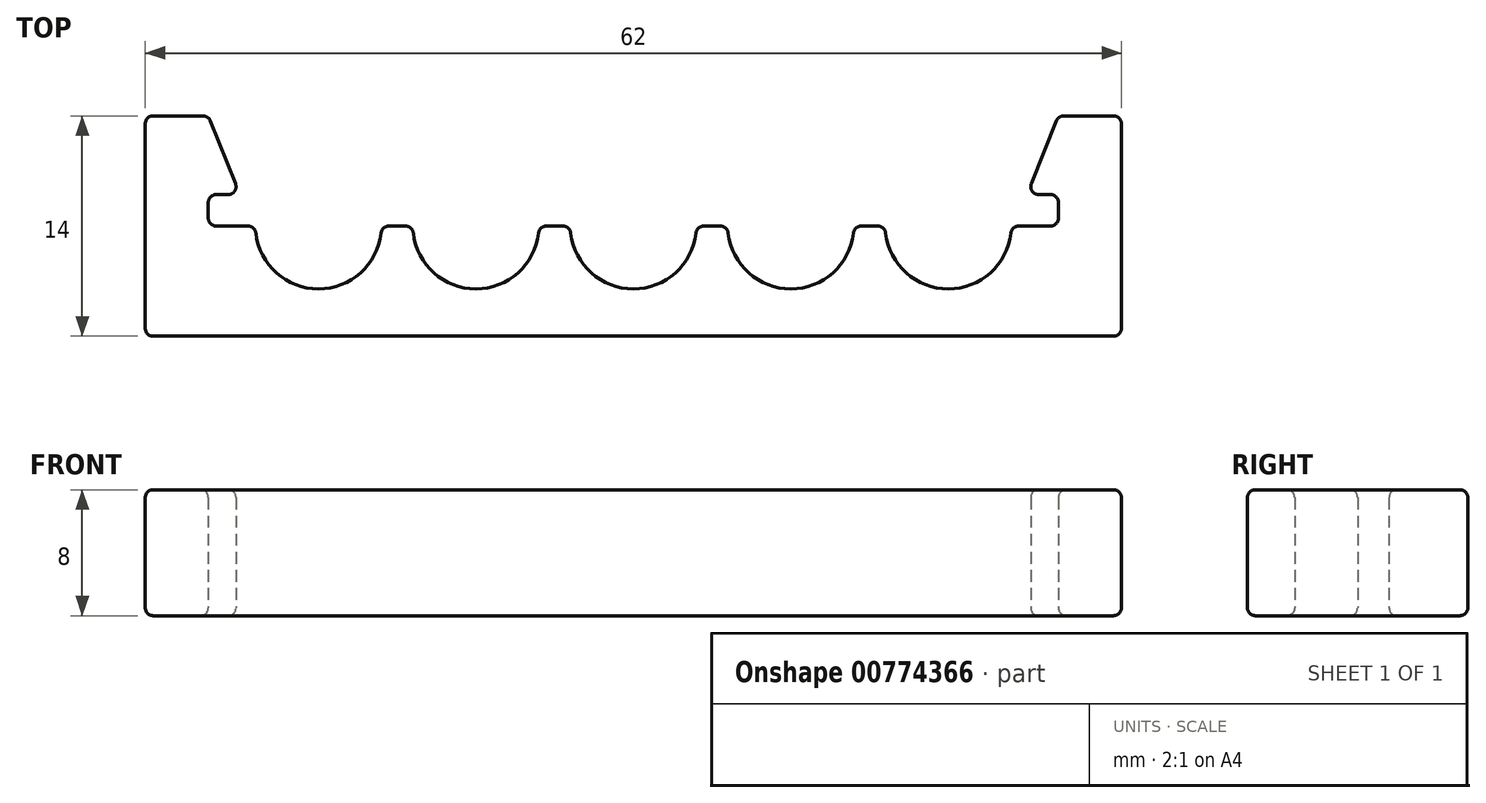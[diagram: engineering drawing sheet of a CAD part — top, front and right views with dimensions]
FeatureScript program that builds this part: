
annotation { "Feature Type Name" : "Feature", "Feature Type Description" : "" }
export const myFeature = defineFeature(function(context is Context, id is Id, definition is map)
    precondition{}
    {
        {
            var Q0;
            Q0=qCreatedBy(makeId("Top.planeOp"),FACE);
            var sketch = newSketch(context, id + "F0", { "sketchPlane" : qUnion([Q0])});
            skArc(sketch, "E0", {"start": v(-3.98, -0.44) * mm, "mid": v(0, -4) * mm, "end": v(3.98, -0.44) * mm});
            skArc(sketch, "E1", {"start": v(6.02, -0.44) * mm, "mid": v(10, -4) * mm, "end": v(13.98, -0.44) * mm});
            skArc(sketch, "E2", {"start": v(16.02, -0.44) * mm, "mid": v(20, -4) * mm, "end": v(23.98, -0.44) * mm});
            skArc(sketch, "E3", {"start": v(-13.98, -0.44) * mm, "mid": v(-10, -4) * mm, "end": v(-6.02, -0.44) * mm});
            skArc(sketch, "E4", {"start": v(-23.98, -0.44) * mm, "mid": v(-20, -4) * mm, "end": v(-16.02, -0.44) * mm});
            skLineSegment(sketch, "E5.bottom", {"start": v(-31, 7) * mm, "end": v(-27, 7) * mm});
            skLineSegment(sketch, "E5.top", {"start": v(-30.5, -7) * mm, "end": v(30.5, -7) * mm});
            skLineSegment(sketch, "E5.left", {"start": v(-31, 7) * mm, "end": v(-31, -6.5) * mm});
            skLineSegment(sketch, "E5.right", {"start": v(31, 6.5) * mm, "end": v(31, -6.5) * mm});
            skLineSegment(sketch, "E6", {"start": v(-26.5, 0) * mm, "end": v(-24.47, 0) * mm});
            skLineSegment(sketch, "E7.bottom", {"start": v(-30.5, 7) * mm, "end": v(-27.34, 7) * mm});
            skLineSegment(sketch, "E7.left", {"start": v(-31, 6.5) * mm, "end": v(-31, 0) * mm});
            skLineSegment(sketch, "E7.right", {"start": v(-27, 1.5) * mm, "end": v(-27, 0.5) * mm});
            skLineSegment(sketch, "E8.bottom", {"start": v(31, 7) * mm, "end": v(27, 7) * mm});
            skLineSegment(sketch, "E8.left", {"start": v(31, 7) * mm, "end": v(31, 0) * mm});
            skLineSegment(sketch, "E8.right", {"start": v(27, 1.5) * mm, "end": v(27, 0.5) * mm});
            skLineSegment(sketch, "E9", {"start": v(-26.87, 6.69) * mm, "end": v(-25.27, 2.69) * mm});
            skLineSegment(sketch, "E10", {"start": v(-25.74, 2) * mm, "end": v(-26.5, 2) * mm});
            skLineSegment(sketch, "E11", {"start": v(26.87, 6.69) * mm, "end": v(25.27, 2.69) * mm});
            skLineSegment(sketch, "E12", {"start": v(25.74, 2) * mm, "end": v(26.5, 2) * mm});
            skLineSegment(sketch, "E13.trimOffspring", {"start": v(27.34, 7) * mm, "end": v(30.5, 7) * mm});
            skPoint(sketch, "E14.orphan", {"position": v(-31, 0) * mm});
            skLineSegment(sketch, "E15.trimOffspring", {"start": v(-15.53, 0) * mm, "end": v(-14.47, 0) * mm});
            skLineSegment(sketch, "E16.trimOffspring", {"start": v(-5.53, 0) * mm, "end": v(-4.47, 0) * mm});
            skLineSegment(sketch, "E17.trimOffspring", {"start": v(4.47, 0) * mm, "end": v(5.53, 0) * mm});
            skLineSegment(sketch, "E18.trimOffspring", {"start": v(14.47, 0) * mm, "end": v(15.53, 0) * mm});
            skLineSegment(sketch, "E19.trimOffspring", {"start": v(24.47, 0) * mm, "end": v(26.5, 0) * mm});
            skPoint(sketch, "E20.orphan", {"position": v(31, 0) * mm});
            skPoint(sketch, "E21.visualSharp", {"position": v(-31, 7) * mm});
            skArc(sketch, "E21.filletArc", {"start": v(-30.5, 7) * mm, "mid": v(-30.85, 6.85) * mm, "end": v(-31, 6.5) * mm});
            skPoint(sketch, "E22.visualSharp", {"position": v(-31, -7) * mm});
            skArc(sketch, "E22.filletArc", {"start": v(-31, -6.5) * mm, "mid": v(-30.85, -6.85) * mm, "end": v(-30.5, -7) * mm});
            skPoint(sketch, "E23.visualSharp", {"position": v(-24, 0) * mm});
            skArc(sketch, "E23.filletArc", {"start": v(-23.98, -0.44) * mm, "mid": v(-24.14, -0.13) * mm, "end": v(-24.47, 0) * mm});
            skPoint(sketch, "E24.visualSharp", {"position": v(-25, 2) * mm});
            skArc(sketch, "E24.filletArc", {"start": v(-25.74, 2) * mm, "mid": v(-25.32, 2.22) * mm, "end": v(-25.27, 2.69) * mm});
            skPoint(sketch, "E25.visualSharp", {"position": v(-27, 0) * mm});
            skArc(sketch, "E25.filletArc", {"start": v(-27, 0.5) * mm, "mid": v(-26.85, 0.15) * mm, "end": v(-26.5, 0) * mm});
            skPoint(sketch, "E26.visualSharp", {"position": v(-27, 2) * mm});
            skArc(sketch, "E26.filletArc", {"start": v(-26.5, 2) * mm, "mid": v(-26.85, 1.85) * mm, "end": v(-27, 1.5) * mm});
            skPoint(sketch, "E27.visualSharp", {"position": v(-16, 0) * mm});
            skArc(sketch, "E27.filletArc", {"start": v(-15.53, 0) * mm, "mid": v(-15.86, -0.13) * mm, "end": v(-16.02, -0.44) * mm});
            skPoint(sketch, "E28.visualSharp", {"position": v(-14, 0) * mm});
            skArc(sketch, "E28.filletArc", {"start": v(-13.98, -0.44) * mm, "mid": v(-14.14, -0.13) * mm, "end": v(-14.47, 0) * mm});
            skPoint(sketch, "E29.visualSharp", {"position": v(-6, 0) * mm});
            skArc(sketch, "E29.filletArc", {"start": v(-5.53, 0) * mm, "mid": v(-5.86, -0.13) * mm, "end": v(-6.02, -0.44) * mm});
            skPoint(sketch, "E30.visualSharp", {"position": v(-4, 0) * mm});
            skArc(sketch, "E30.filletArc", {"start": v(-3.98, -0.44) * mm, "mid": v(-4.14, -0.13) * mm, "end": v(-4.47, 0) * mm});
            skPoint(sketch, "E31.visualSharp", {"position": v(4, 0) * mm});
            skArc(sketch, "E31.filletArc", {"start": v(4.47, 0) * mm, "mid": v(4.14, -0.13) * mm, "end": v(3.98, -0.44) * mm});
            skPoint(sketch, "E32.visualSharp", {"position": v(6, 0) * mm});
            skArc(sketch, "E32.filletArc", {"start": v(6.02, -0.44) * mm, "mid": v(5.86, -0.13) * mm, "end": v(5.53, 0) * mm});
            skPoint(sketch, "E33.visualSharp", {"position": v(14, 0) * mm});
            skArc(sketch, "E33.filletArc", {"start": v(14.47, 0) * mm, "mid": v(14.14, -0.13) * mm, "end": v(13.98, -0.44) * mm});
            skPoint(sketch, "E34.visualSharp", {"position": v(16, 0) * mm});
            skArc(sketch, "E34.filletArc", {"start": v(16.02, -0.44) * mm, "mid": v(15.86, -0.13) * mm, "end": v(15.53, 0) * mm});
            skPoint(sketch, "E35.visualSharp", {"position": v(24, 0) * mm});
            skArc(sketch, "E35.filletArc", {"start": v(24.47, 0) * mm, "mid": v(24.14, -0.13) * mm, "end": v(23.98, -0.44) * mm});
            skPoint(sketch, "E36.visualSharp", {"position": v(27, 0) * mm});
            skArc(sketch, "E36.filletArc", {"start": v(26.5, 0) * mm, "mid": v(26.85, 0.15) * mm, "end": v(27, 0.5) * mm});
            skPoint(sketch, "E37.visualSharp", {"position": v(27, 2) * mm});
            skArc(sketch, "E37.filletArc", {"start": v(27, 1.5) * mm, "mid": v(26.85, 1.85) * mm, "end": v(26.5, 2) * mm});
            skPoint(sketch, "E38.visualSharp", {"position": v(25, 2) * mm});
            skArc(sketch, "E38.filletArc", {"start": v(25.27, 2.69) * mm, "mid": v(25.32, 2.22) * mm, "end": v(25.74, 2) * mm});
            skPoint(sketch, "E39.visualSharp", {"position": v(31, -7) * mm});
            skArc(sketch, "E39.filletArc", {"start": v(30.5, -7) * mm, "mid": v(30.85, -6.85) * mm, "end": v(31, -6.5) * mm});
            skPoint(sketch, "E40.visualSharp", {"position": v(31, 7) * mm});
            skArc(sketch, "E40.filletArc", {"start": v(31, 6.5) * mm, "mid": v(30.85, 6.85) * mm, "end": v(30.5, 7) * mm});
            skPoint(sketch, "E41.visualSharp", {"position": v(27, 7) * mm});
            skArc(sketch, "E41.filletArc", {"start": v(27.34, 7) * mm, "mid": v(27.06, 6.91) * mm, "end": v(26.87, 6.69) * mm});
            skPoint(sketch, "E42.visualSharp", {"position": v(-27, 7) * mm});
            skArc(sketch, "E42.filletArc", {"start": v(-26.87, 6.69) * mm, "mid": v(-27.06, 6.91) * mm, "end": v(-27.34, 7) * mm});
            skSolve(sketch);
        }
        {
            var Q0;
            Q0 = qSketchRegion(id + "F0", true);
            extrude(context, id + "F1", {"entities" : qUnion([Q0]), "depth" : 8 * mm, "offsetDistance" : 25 * mm});
        }
        {
            var Q0;
            Q0=makeQuery(id+"F1.opExtrude","SWEPT_FACE",FACE,{"disambiguationData":[OSD([sQuery(id+"F0.wireOp",EDGE,"E5.right"),sQuery(id+"F0.wireOp",EDGE,"E8.left")])]});
            var Q1;
            Q1=makeQuery(id+"F1.opExtrude","CAP_FACE",FACE,{"disambiguationData":[OSD([sQuery(id+"F0.wireOp",EDGE,"E0"),sQuery(id+"F0.wireOp",EDGE,"E1"),sQuery(id+"F0.wireOp",EDGE,"E2"),sQuery(id+"F0.wireOp",EDGE,"E3"),sQuery(id+"F0.wireOp",EDGE,"E4"),sQuery(id+"F0.wireOp",EDGE,"E5.bottom"),sQuery(id+"F0.wireOp",EDGE,"E5.top"),sQuery(id+"F0.wireOp",EDGE,"E5.left"),sQuery(id+"F0.wireOp",EDGE,"E5.right"),sQuery(id+"F0.wireOp",EDGE,"E6"),sQuery(id+"F0.wireOp",EDGE,"E7.bottom"),sQuery(id+"F0.wireOp",EDGE,"E7.left"),sQuery(id+"F0.wireOp",EDGE,"E7.right"),sQuery(id+"F0.wireOp",EDGE,"E8.bottom"),sQuery(id+"F0.wireOp",EDGE,"E8.left"),sQuery(id+"F0.wireOp",EDGE,"E8.right"),sQuery(id+"F0.wireOp",EDGE,"E9"),sQuery(id+"F0.wireOp",EDGE,"E10"),sQuery(id+"F0.wireOp",EDGE,"E11"),sQuery(id+"F0.wireOp",EDGE,"E12"),sQuery(id+"F0.wireOp",EDGE,"E13.trimOffspring"),sQuery(id+"F0.wireOp",EDGE,"E15.trimOffspring"),sQuery(id+"F0.wireOp",EDGE,"E16.trimOffspring"),sQuery(id+"F0.wireOp",EDGE,"E17.trimOffspring"),sQuery(id+"F0.wireOp",EDGE,"E18.trimOffspring"),sQuery(id+"F0.wireOp",EDGE,"E19.trimOffspring"),sQuery(id+"F0.wireOp",EDGE,"E22.filletArc"),sQuery(id+"F0.wireOp",EDGE,"E23.filletArc"),sQuery(id+"F0.wireOp",EDGE,"E24.filletArc"),sQuery(id+"F0.wireOp",EDGE,"E25.filletArc"),sQuery(id+"F0.wireOp",EDGE,"E26.filletArc"),sQuery(id+"F0.wireOp",EDGE,"E27.filletArc"),sQuery(id+"F0.wireOp",EDGE,"E28.filletArc"),sQuery(id+"F0.wireOp",EDGE,"E29.filletArc"),sQuery(id+"F0.wireOp",EDGE,"E30.filletArc"),sQuery(id+"F0.wireOp",EDGE,"E31.filletArc"),sQuery(id+"F0.wireOp",EDGE,"E32.filletArc"),sQuery(id+"F0.wireOp",EDGE,"E33.filletArc"),sQuery(id+"F0.wireOp",EDGE,"E34.filletArc"),sQuery(id+"F0.wireOp",EDGE,"E35.filletArc"),sQuery(id+"F0.wireOp",EDGE,"E36.filletArc"),sQuery(id+"F0.wireOp",EDGE,"E37.filletArc"),sQuery(id+"F0.wireOp",EDGE,"E38.filletArc"),sQuery(id+"F0.wireOp",EDGE,"E39.filletArc"),sQuery(id+"F0.wireOp",EDGE,"E41.filletArc"),sQuery(id+"F0.wireOp",EDGE,"E42.filletArc")])],"isStart":false});
            var Q2;
            Q2=makeQuery(id+"F1.opExtrude","CAP_FACE",FACE,{"disambiguationData":[OSD([sQuery(id+"F0.wireOp",EDGE,"E0"),sQuery(id+"F0.wireOp",EDGE,"E1"),sQuery(id+"F0.wireOp",EDGE,"E2"),sQuery(id+"F0.wireOp",EDGE,"E3"),sQuery(id+"F0.wireOp",EDGE,"E4"),sQuery(id+"F0.wireOp",EDGE,"E5.bottom"),sQuery(id+"F0.wireOp",EDGE,"E5.top"),sQuery(id+"F0.wireOp",EDGE,"E5.left"),sQuery(id+"F0.wireOp",EDGE,"E5.right"),sQuery(id+"F0.wireOp",EDGE,"E6"),sQuery(id+"F0.wireOp",EDGE,"E7.bottom"),sQuery(id+"F0.wireOp",EDGE,"E7.left"),sQuery(id+"F0.wireOp",EDGE,"E7.right"),sQuery(id+"F0.wireOp",EDGE,"E8.bottom"),sQuery(id+"F0.wireOp",EDGE,"E8.left"),sQuery(id+"F0.wireOp",EDGE,"E8.right"),sQuery(id+"F0.wireOp",EDGE,"E9"),sQuery(id+"F0.wireOp",EDGE,"E10"),sQuery(id+"F0.wireOp",EDGE,"E11"),sQuery(id+"F0.wireOp",EDGE,"E12"),sQuery(id+"F0.wireOp",EDGE,"E13.trimOffspring"),sQuery(id+"F0.wireOp",EDGE,"E15.trimOffspring"),sQuery(id+"F0.wireOp",EDGE,"E16.trimOffspring"),sQuery(id+"F0.wireOp",EDGE,"E17.trimOffspring"),sQuery(id+"F0.wireOp",EDGE,"E18.trimOffspring"),sQuery(id+"F0.wireOp",EDGE,"E19.trimOffspring"),sQuery(id+"F0.wireOp",EDGE,"E22.filletArc"),sQuery(id+"F0.wireOp",EDGE,"E23.filletArc"),sQuery(id+"F0.wireOp",EDGE,"E24.filletArc"),sQuery(id+"F0.wireOp",EDGE,"E25.filletArc"),sQuery(id+"F0.wireOp",EDGE,"E26.filletArc"),sQuery(id+"F0.wireOp",EDGE,"E27.filletArc"),sQuery(id+"F0.wireOp",EDGE,"E28.filletArc"),sQuery(id+"F0.wireOp",EDGE,"E29.filletArc"),sQuery(id+"F0.wireOp",EDGE,"E30.filletArc"),sQuery(id+"F0.wireOp",EDGE,"E31.filletArc"),sQuery(id+"F0.wireOp",EDGE,"E32.filletArc"),sQuery(id+"F0.wireOp",EDGE,"E33.filletArc"),sQuery(id+"F0.wireOp",EDGE,"E34.filletArc"),sQuery(id+"F0.wireOp",EDGE,"E35.filletArc"),sQuery(id+"F0.wireOp",EDGE,"E36.filletArc"),sQuery(id+"F0.wireOp",EDGE,"E37.filletArc"),sQuery(id+"F0.wireOp",EDGE,"E38.filletArc"),sQuery(id+"F0.wireOp",EDGE,"E39.filletArc"),sQuery(id+"F0.wireOp",EDGE,"E41.filletArc"),sQuery(id+"F0.wireOp",EDGE,"E42.filletArc")])],"isStart":true});
            var Q3;
            Q3=makeQuery(id+"F1.opExtrude","SWEPT_FACE",FACE,{"disambiguationData":[OSD([sQuery(id+"F0.wireOp",EDGE,"E5.left"),sQuery(id+"F0.wireOp",EDGE,"E7.left")])]});
            fillet(context, id + "F2", {"entities" : qUnion([Q0, Q1, Q2, Q3]), "radius" : .5 * mm, "tangentPropagation" : true, "allowEdgeOverflow" : false});
        }
    });
